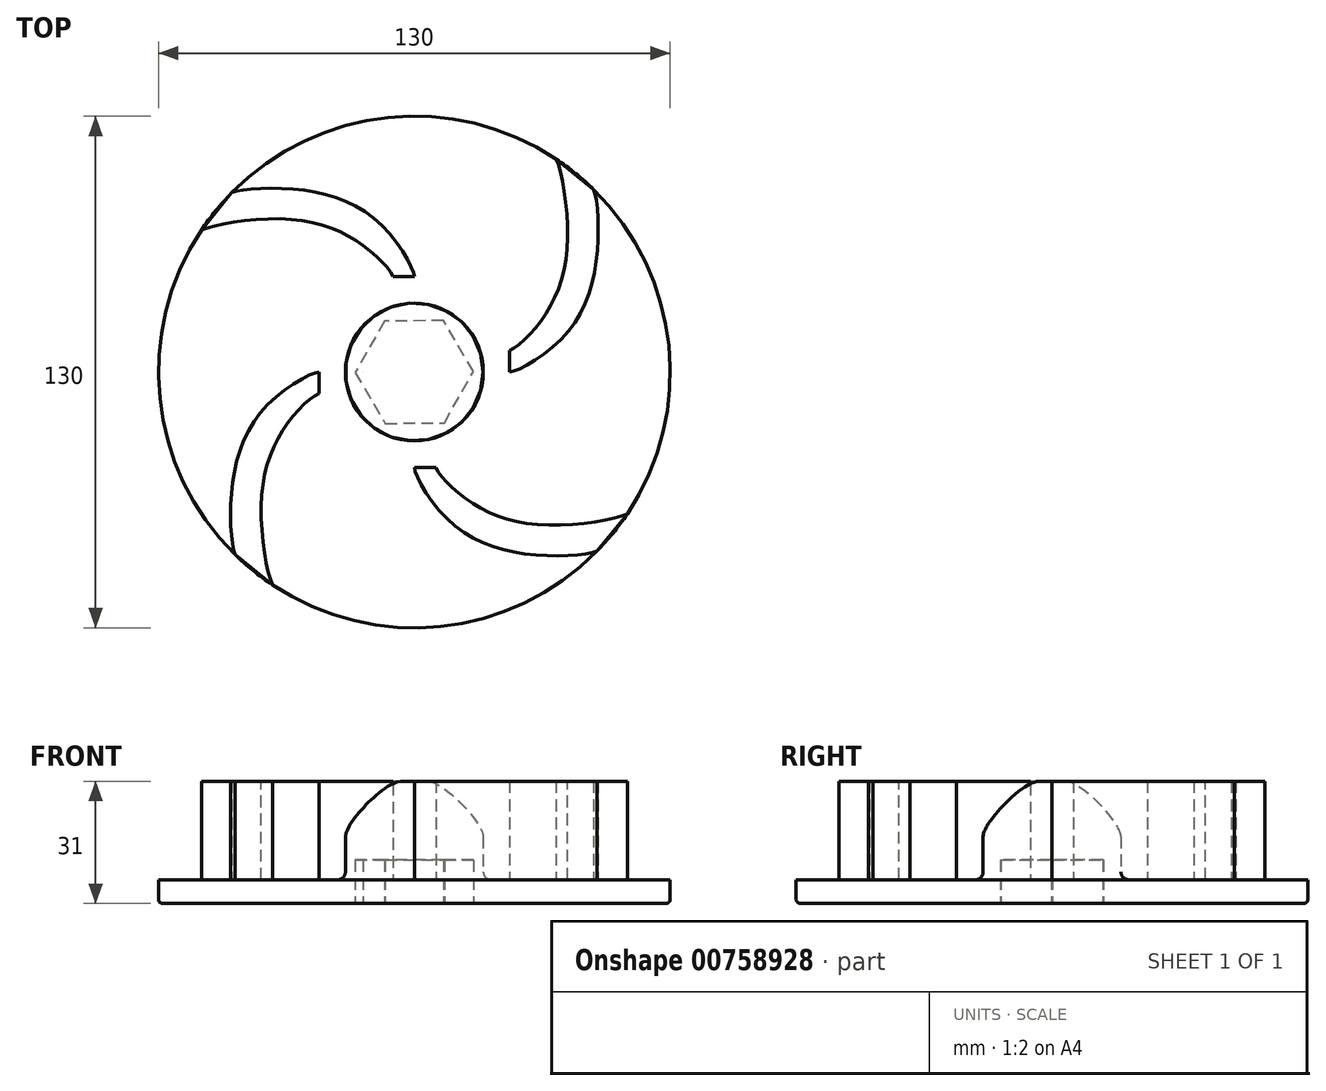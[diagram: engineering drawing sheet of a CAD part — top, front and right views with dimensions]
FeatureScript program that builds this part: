
annotation { "Feature Type Name" : "Feature", "Feature Type Description" : "" }
export const myFeature = defineFeature(function(context is Context, id is Id, definition is map)
    precondition{}
    {
        {
            var Q0;
            Q0=qCreatedBy(makeId("Top.planeOp"),FACE);
            var sketch = newSketch(context, id + "F0", { "sketchPlane" : qUnion([Q0])});
            skCircle(sketch, "E0", {"center": v(0, 0) * mm, "radius": 65 * mm});
            skSolve(sketch);
        }
        {
            var Q0;
            Q0=makeQuery(id+"F0.imprint","IMPRINT",FACE,{"disambiguationData":[TD([[makeQuery(id+"F0.imprint","IMPRINT",EDGE,{"derivedFrom":sQuery(id+"F0.wireOp",EDGE,"E0")}),1.0]])]});
            extrude(context, id + "F1", {"entities" : qUnion([Q0]), "depth" : 6 * mm, "offsetDistance" : 25 * mm});
        }
        {
            var Q0;
            Q0=makeQuery(id+"F1.opExtrude","CAP_FACE",FACE,{"disambiguationData":[OSD([sQuery(id+"F0.wireOp",EDGE,"E0")])],"isStart":false});
            var sketch = newSketch(context, id + "F2", { "sketchPlane" : qUnion([Q0])});
            skFitSpline(sketch, "E1", {"points": [v(0, 24.22) * mm, v(-8.48, 37.47) * mm, v(-30.34, 46.43) * mm, v(-46.39, 45.53) * mm], "startDerivative": vector(0, 16.64) * mm, "endDerivative": vector(-20.88, -9.42) * mm});
            skFitSpline(sketch, "E2", {"points": [v(-5.45, 24.22) * mm, v(-13.32, 32.39) * mm, v(-32.54, 38.87) * mm, v(-54.1, 36.04) * mm], "startDerivative": vector(-10.27, 24) * mm, "endDerivative": vector(-26.07, -11.97) * mm});
            skLineSegment(sketch, "E3", {"start": v(-54.1, 36.04) * mm, "end": v(-46.39, 45.53) * mm});
            skLineSegment(sketch, "E4", {"start": v(-5.45, 24.22) * mm, "end": v(0, 24.22) * mm});
            skSolve(sketch);
        }
        {
            var Q0;
            Q0=qSketchRegion(id+"F2",true);
            extrude(context, id + "F3", {"entities" : qUnion([Q0]), "operationType" : NewBodyOperationType.ADD, "depth" : 25 * mm, "offsetDistance" : 25 * mm});
        }
        {
            var Q0;
            Q0=qCreatedBy(makeId("Front.planeOp"),FACE);
            var sketch = newSketch(context, id + "F4", { "sketchPlane" : qUnion([Q0])});
            skLineSegment(sketch, "E5", {"start": v(0, 0) * mm, "end": v(0, 45.71) * mm, "construction": true});
            skSolve(sketch);
        }
        {
            var Q0;
            Q0=makeQuery(id+"F1.opExtrude","SWEPT_BODY",BODY,{"disambiguationData":[OSD([sQuery(id+"F0.wireOp",EDGE,"E0")])]});
            var Q1;
            Q1=sQuery(id+"F4.wireOp",EDGE,"E5");
            circularPattern(context, id + "F5", {"entities" : qUnion([Q0]), "axis" : qUnion([Q1]), "angle" : 360 * degree, "instanceCount" : 4, "equalSpace" : true});
        }
        {
            var Q0;
            Q0=makeQuery(id+"F5.opPattern","COPY",FACE,{"derivedFrom":makeQuery(id+"F1.opExtrude","CAP_FACE",FACE,{"disambiguationData":[OSD([sQuery(id+"F0.wireOp",EDGE,"E0")])],"isStart":false}),"instanceName":"1"});
            var sketch = newSketch(context, id + "F6", { "sketchPlane" : qUnion([Q0])});
            skCircle(sketch, "E6", {"center": v(0, 0) * mm, "radius": 17.5 * mm});
            skSolve(sketch);
        }
        {
            var Q0;
            Q0=qSketchRegion(id+"F6",true);
            var Q1;
            Q1=sQuery(id+"F6.wireOp",EDGE,"E6");
            extrude(context, id + "F7", {"entities" : qUnion([Q0]), "operationType" : NewBodyOperationType.ADD, "surfaceEntities" : qUnion([Q1]), "depth" : 25 * mm, "offsetDistance" : 25 * mm});
        }
        {
            var Q0;
            Q0=makeQuery(id+"F1.opExtrude","CAP_EDGE",EDGE,{"disambiguationData":[OSD([sQuery(id+"F0.wireOp",EDGE,"E0")])],"isStart":true});
            fillet(context, id + "F8", {"entities" : qUnion([Q0]), "radius" : 1 * mm, "tangentPropagation" : true, "allowEdgeOverflow" : false});
        }
        {
            var Q0;
            {var subQ0=sQuery(id+"F0.wireOp",EDGE,"E0");var subQ1=makeQuery(id+"F1.opExtrude","CAP_FACE",FACE,{"disambiguationData":[OSD([subQ0])],"isStart":false});var subQ2=makeQuery(id+"F3.boolean.opBoolean","SPLIT",FACE,{"disambiguationData":[TD([makeQuery(id+"F1.opExtrude","SWEPT_FACE",FACE,{"disambiguationData":[OSD([subQ0])]}),subQ1,makeQuery(id+"F3.opExtrude","SWEPT_FACE",FACE,{"disambiguationData":[OSD([sQuery(id+"F2.wireOp",EDGE,"E1")])]}),makeQuery(id+"F3.opExtrude","SWEPT_FACE",FACE,{"disambiguationData":[OSD([sQuery(id+"F2.wireOp",EDGE,"E2")])]}),makeQuery(id+"F3.opExtrude","SWEPT_FACE",FACE,{"disambiguationData":[OSD([sQuery(id+"F2.wireOp",EDGE,"E3")])]}),makeQuery(id+"F3.opExtrude","SWEPT_FACE",FACE,{"disambiguationData":[OSD([sQuery(id+"F2.wireOp",EDGE,"E4")])]})])],"derivedFrom":subQ1});Q0=makeQuery(id+"F7.boolean.opBoolean","INTERSECT",EDGE,{"derivedFrom":[subQ2,makeQuery(id+"F5.opPattern","COPY",FACE,{"derivedFrom":subQ2,"instanceName":"1"}),makeQuery(id+"F5.opPattern","COPY",FACE,{"derivedFrom":subQ2,"instanceName":"2"}),makeQuery(id+"F5.opPattern","COPY",FACE,{"derivedFrom":subQ2,"instanceName":"3"}),makeQuery(id+"F5.opPattern","COPY",FACE,{"derivedFrom":subQ2,"instanceName":"4"}),makeQuery(id+"F5.opPattern","COPY",FACE,{"derivedFrom":subQ2,"instanceName":"5"}),makeQuery(id+"F5.opPattern","COPY",FACE,{"derivedFrom":subQ2,"instanceName":"6"})]});}
            fillet(context, id + "F9", {"entities" : qUnion([Q0]), "radius" : 2 * mm, "tangentPropagation" : true, "allowEdgeOverflow" : false});
        }
        {
            var Q0;
            Q0=makeQuery(id+"F7.opExtrude","CAP_EDGE",EDGE,{"disambiguationData":[OSD([sQuery(id+"F6.wireOp",EDGE,"E6")])],"isStart":false});
            fillet(context, id + "F10", {"entities" : qUnion([Q0]), "radius" : 14 * mm, "tangentPropagation" : true, "rho" : 0.2, "crossSection" : FilletCrossSection.CONIC, "allowEdgeOverflow" : false});
        }
        {
            var Q0;
            Q0=makeQuery(id+"F1.opExtrude","CAP_FACE",FACE,{"disambiguationData":[OSD([sQuery(id+"F0.wireOp",EDGE,"E0")])],"isStart":true});
            var sketch = newSketch(context, id + "F11", { "sketchPlane" : qUnion([Q0])});
            skCircle(sketch, "E7.cCircle", {"center": v(0, 0) * mm, "radius": 13 * mm, "construction": true});
            skLineSegment(sketch, "E7.0", {"start": v(15.01, -0.13) * mm, "end": v(7.4, -13.06) * mm});
            skLineSegment(sketch, "E7.1", {"start": v(7.4, -13.06) * mm, "end": v(-7.62, -12.94) * mm});
            skLineSegment(sketch, "E7.2", {"start": v(-7.62, -12.94) * mm, "end": v(-15.01, 0.13) * mm});
            skLineSegment(sketch, "E7.3", {"start": v(-15.01, 0.13) * mm, "end": v(-7.4, 13.06) * mm});
            skLineSegment(sketch, "E7.4", {"start": v(-7.4, 13.06) * mm, "end": v(7.62, 12.94) * mm});
            skLineSegment(sketch, "E7.5", {"start": v(7.62, 12.94) * mm, "end": v(15.01, -0.13) * mm});
            skPoint(sketch, "E7.0.midPoint", {"position": v(11.2, -6.6) * mm});
            skCircle(sketch, "E8.cCircle", {"center": v(-13, 0) * mm, "radius": 0 * mm, "construction": true});
            skLineSegment(sketch, "E8.0", {"start": v(-13, 0) * mm, "end": v(-13, 0) * mm});
            skLineSegment(sketch, "E8.1", {"start": v(-13, 0) * mm, "end": v(-13, 0) * mm});
            skLineSegment(sketch, "E8.2", {"start": v(-13, 0) * mm, "end": v(-13, 0) * mm});
            skLineSegment(sketch, "E8.3", {"start": v(-13, 0) * mm, "end": v(-13, 0) * mm});
            skLineSegment(sketch, "E8.4", {"start": v(-13, 0) * mm, "end": v(-13, 0) * mm});
            skLineSegment(sketch, "E8.5", {"start": v(-13, 0) * mm, "end": v(-13, 0) * mm});
            skPoint(sketch, "E8.0.midPoint", {"position": v(-13, 0) * mm});
            skSolve(sketch);
        }
        {
            var Q0;
            Q0=makeQuery(id+"F11.imprint","IMPRINT",FACE,{"disambiguationData":[TD([[makeQuery(id+"F11.imprint","IMPRINT",EDGE,{"derivedFrom":sQuery(id+"F11.wireOp",EDGE,"E7.0")}),-1.0]])]});
            extrude(context, id + "F12", {"entities" : qUnion([Q0]), "operationType" : NewBodyOperationType.REMOVE, "oppositeDirection" : true, "depth" : 11 * mm, "offsetDistance" : 25 * mm});
        }
    });
